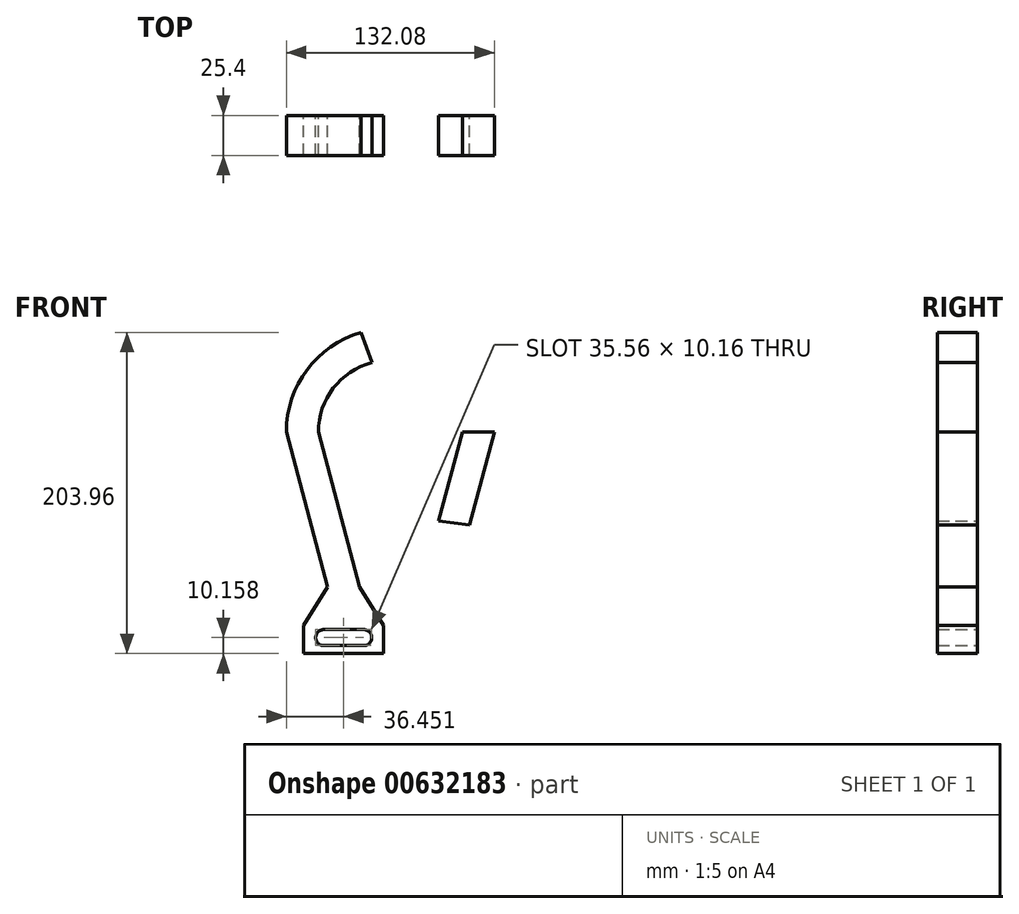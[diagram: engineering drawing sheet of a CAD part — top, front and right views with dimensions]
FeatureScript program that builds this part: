
annotation { "Feature Type Name" : "Feature", "Feature Type Description" : "" }
export const myFeature = defineFeature(function(context is Context, id is Id, definition is map)
    precondition{}
    {
        {
            var Q0;
            Q0=qCreatedBy(makeId("Front.planeOp"),FACE);
            var sketch = newSketch(context, id + "F0", { "sketchPlane" : qUnion([Q0])});
            skLineSegment(sketch, "E0", {"start": v(27.4, -47.07) * mm, "end": v(1.1, 51.07) * mm});
            skLineSegment(sketch, "E1", {"start": v(47.72, -47.07) * mm, "end": v(21.43, 51.07) * mm});
            skLineSegment(sketch, "E2", {"start": v(21.43, 51.07) * mm, "end": v(1.1, 51.07) * mm});
            skLineSegment(sketch, "E3", {"start": v(54.33, -71.75) * mm, "end": v(34.01, -71.75) * mm});
            skLineSegment(sketch, "E4", {"start": v(27.4, -47.07) * mm, "end": v(12.16, -71.75) * mm});
            skLineSegment(sketch, "E5", {"start": v(47.72, -47.07) * mm, "end": v(62.96, -71.75) * mm});
            skLineSegment(sketch, "E6", {"start": v(34.01, -71.75) * mm, "end": v(12.16, -71.75) * mm});
            skLineSegment(sketch, "E7", {"start": v(54.33, -71.75) * mm, "end": v(62.96, -71.75) * mm});
            skLineSegment(sketch, "E8", {"start": v(47.72, -47.07) * mm, "end": v(27.4, -47.07) * mm});
            skLineSegment(sketch, "E9", {"start": v(12.16, -71.75) * mm, "end": v(12.16, -89.53) * mm});
            skLineSegment(sketch, "E10", {"start": v(12.16, -89.53) * mm, "end": v(62.96, -89.53) * mm});
            skLineSegment(sketch, "E11", {"start": v(62.96, -89.53) * mm, "end": v(62.96, -71.75) * mm});
            skCircle(sketch, "E12", {"center": v(24.86, -79.37) * mm, "radius": 5.08 * mm});
            skLineSegment(sketch, "E13", {"start": v(24.86, -79.37) * mm, "end": v(24.86, -71.75) * mm});
            skCircle(sketch, "E14", {"center": v(50.26, -79.37) * mm, "radius": 5.08 * mm});
            skLineSegment(sketch, "E15", {"start": v(50.26, -79.37) * mm, "end": v(50.26, -71.75) * mm});
            skLineSegment(sketch, "E16", {"start": v(24.86, -74.3) * mm, "end": v(50.26, -74.3) * mm});
            skLineSegment(sketch, "E17", {"start": v(24.86, -79.37) * mm, "end": v(24.86, -89.53) * mm});
            skLineSegment(sketch, "E18", {"start": v(50.26, -79.37) * mm, "end": v(50.26, -89.53) * mm});
            skLineSegment(sketch, "E19", {"start": v(24.86, -84.45) * mm, "end": v(50.26, -84.45) * mm});
            skLineSegment(sketch, "E20", {"start": v(21.43, 51.07) * mm, "end": v(67.15, 51.07) * mm});
            skLineSegment(sketch, "E21", {"start": v(67.15, 51.07) * mm, "end": v(112.87, 51.07) * mm});
            skArc(sketch, "E22", {"start": v(1.1, 51.07) * mm, "mid": v(67.15, 117.1) * mm, "end": v(133.19, 51.07) * mm});
            skLineSegment(sketch, "E23", {"start": v(133.19, 51.07) * mm, "end": v(112.87, 51.07) * mm});
            skArc(sketch, "E24", {"start": v(21.43, 51.07) * mm, "mid": v(67.15, 96.79) * mm, "end": v(112.87, 51.07) * mm});
            skLineSegment(sketch, "E25", {"start": v(112.87, 51.07) * mm, "end": v(97.74, -5.36) * mm});
            skLineSegment(sketch, "E26", {"start": v(133.19, 51.07) * mm, "end": v(117.4, -7.82) * mm});
            skLineSegment(sketch, "E27", {"start": v(97.74, -5.36) * mm, "end": v(117.4, -7.82) * mm});
            skLineSegment(sketch, "E28", {"start": v(112.87, 51.07) * mm, "end": v(112.87, 30.87) * mm});
            skLineSegment(sketch, "E29", {"start": v(133.19, 51.07) * mm, "end": v(133.19, 30.74) * mm});
            skLineSegment(sketch, "E30", {"start": v(81.2, 94.57) * mm, "end": v(88.15, 113.68) * mm});
            skLineSegment(sketch, "E31", {"start": v(55.52, 95.28) * mm, "end": v(48.55, 114.43) * mm});
            skSolve(sketch);
        }
        {
            var Q0;
            Q0=makeQuery(id+"F0.imprint","IMPRINT",FACE,{"disambiguationData":[TD([[makeQuery(id+"F0.imprint","IMPRINT",EDGE,{"derivedFrom":sQuery(id+"F0.wireOp",EDGE,"E2")}),-1.0]])]});
            var Q1;
            Q1=makeQuery(id+"F0.imprint","IMPRINT",FACE,{"disambiguationData":[TD([[makeQuery(id+"F0.imprint","IMPRINT",EDGE,{"derivedFrom":sQuery(id+"F0.wireOp",EDGE,"E23")}),1.0]])]});
            var Q2;
            Q2=makeQuery(id+"F0.imprint","IMPRINT",FACE,{"disambiguationData":[TD([[makeQuery(id+"F0.imprint","IMPRINT",EDGE,{"derivedFrom":sQuery(id+"F0.wireOp",EDGE,"E0")}),-1.0]])]});
            var Q3;
            {var subQ0=sQuery(id+"F0.wireOp",EDGE,"E4");Q3=makeQuery(id+"F0.imprint","IMPRINT",FACE,{"disambiguationData":[TD([[makeQuery(id+"F0.imprint","IMPRINT",EDGE,{"derivedFrom":subQ0}),1.0]])]});}
            var Q4;
            {var subQ1=sQuery(id+"F0.wireOp",EDGE,"E9");Q4=makeQuery(id+"F0.imprint","IMPRINT",FACE,{"disambiguationData":[TD([[makeQuery(id+"F0.imprint","IMPRINT",EDGE,{"derivedFrom":subQ1}),1.0]])]});}
            var Q5;
            {var subQ5=sQuery(id+"F0.wireOp",EDGE,"E19");Q5=makeQuery(id+"F0.imprint","IMPRINT",FACE,{"disambiguationData":[TD([[makeQuery(id+"F0.imprint","IMPRINT",EDGE,{"derivedFrom":subQ5}),-1.0]])]});}
            var Q6;
            {var subQ4=sQuery(id+"F0.wireOp",EDGE,"E7");Q6=makeQuery(id+"F0.imprint","IMPRINT",FACE,{"disambiguationData":[TD([[makeQuery(id+"F0.imprint","IMPRINT",EDGE,{"derivedFrom":subQ4}),-1.0]])]});}
            var Q7;
            {var subQ3=sQuery(id+"F0.wireOp",EDGE,"E16");Q7=makeQuery(id+"F0.imprint","IMPRINT",FACE,{"disambiguationData":[TD([[makeQuery(id+"F0.imprint","IMPRINT",EDGE,{"derivedFrom":subQ3}),1.0]])]});}
            extrude(context, id + "F1", {"entities" : qUnion([Q0, Q1, Q2, Q3, Q4, Q5, Q6, Q7]), "depth" : 25.4 * mm, "offsetDistance" : 25.4 * mm});
        }
    });
